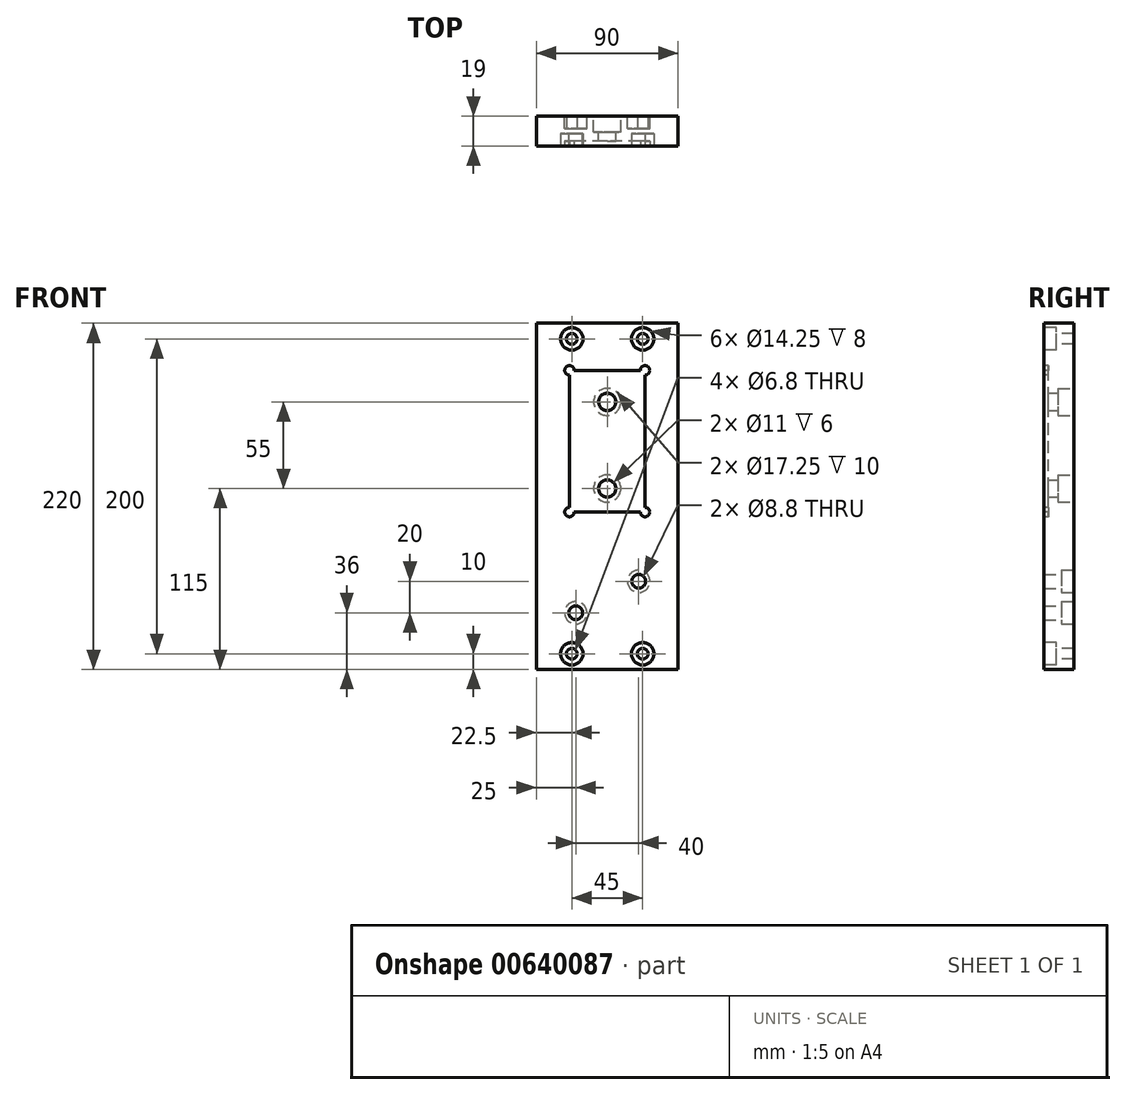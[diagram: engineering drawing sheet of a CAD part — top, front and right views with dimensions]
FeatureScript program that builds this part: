
annotation { "Feature Type Name" : "Feature", "Feature Type Description" : "" }
export const myFeature = defineFeature(function(context is Context, id is Id, definition is map)
    precondition{}
    {
        {
            var Q0;
            Q0=qCreatedBy(makeId("Front.planeOp"),FACE);
            var sketch = newSketch(context, id + "F0", { "sketchPlane" : qUnion([Q0])});
            skLineSegment(sketch, "E0.bottom", {"start": v(0, 0) * mm, "end": v(90, 0) * mm});
            skLineSegment(sketch, "E0.top", {"start": v(0, 220) * mm, "end": v(90, 220) * mm});
            skLineSegment(sketch, "E0.left", {"start": v(0, 0) * mm, "end": v(0, 220) * mm});
            skLineSegment(sketch, "E0.right", {"start": v(90, 0) * mm, "end": v(90, 220) * mm});
            skSolve(sketch);
        }
        {
            var Q0;
            Q0 = qSketchRegion(id + "F0", true);
            extrude(context, id + "F1", {"entities" : qUnion([Q0]), "depth" : 19 * mm, "offsetDistance" : 25 * mm});
        }
        {
            var Q0;
            Q0=makeQuery(id+"F1.opExtrude","CAP_FACE",FACE,{"disambiguationData":[OSD([sQuery(id+"F0.wireOp",EDGE,"E0.bottom"),sQuery(id+"F0.wireOp",EDGE,"E0.top"),sQuery(id+"F0.wireOp",EDGE,"E0.left"),sQuery(id+"F0.wireOp",EDGE,"E0.right")])],"isStart":false});
            var sketch = newSketch(context, id + "F2", { "sketchPlane" : qUnion([Q0])});
            skPoint(sketch, "E1", {"position": v(22.5, 210) * mm});
            skPoint(sketch, "E2", {"position": v(67.5, 210) * mm});
            skPoint(sketch, "E3", {"position": v(22.5, 10) * mm});
            skPoint(sketch, "E4", {"position": v(67.5, 10) * mm});
            skSolve(sketch);
        }
        {
            var Q0;
            Q0=sQuery(id+"F2.wireOp",VERTEX,"E1");
            var Q1;
            Q1=sQuery(id+"F2.wireOp",VERTEX,"E2");
            var Q2;
            Q2=sQuery(id+"F2.wireOp",VERTEX,"E3");
            var Q3;
            Q3=sQuery(id+"F2.wireOp",VERTEX,"E4");
            var Q4;
            Q4=makeQuery(id+"F1.opExtrude","SWEPT_BODY",BODY,{"disambiguationData":[OSD([sQuery(id+"F0.wireOp",EDGE,"E0.bottom"),sQuery(id+"F0.wireOp",EDGE,"E0.top"),sQuery(id+"F0.wireOp",EDGE,"E0.left"),sQuery(id+"F0.wireOp",EDGE,"E0.right")])]});
            hole(context, id + "F3", {"style" : HoleStyle.C_BORE, "endStyle" : HoleEndStyle.THROUGH, "standardTappedOrClearance" : lookupTablePath({ "standard" : "ISO", "engagement" : "75%", "pitch" : "1.25 mm", "size" : "M8", "type" : "Tapped" }), "standardBlindInLast" : lookupTablePath({ "standard" : "ISO", "engagement" : "75%", "pitch" : "1.25 mm", "size" : "M8", "type" : "Tapped" }), "holeDiameter" : 6.8 * mm, "cBoreDiameter" : 14.25 * mm, "cBoreDepth" : 8 * mm, "majorDiameter" : 8 * mm, "showTappedDepth" : true, "isTappedThrough" : true, "tappedDepth" : 14.5 * mm, "tapClearance" : 3, "startFromSketch" : true, "locations" : qUnion([Q0, Q1, Q2, Q3]), "scope" : qUnion([Q4])});
        }
        {
            var Q0;
            Q0=makeQuery(id+"F1.opExtrude","CAP_FACE",FACE,{"disambiguationData":[OSD([sQuery(id+"F0.wireOp",EDGE,"E0.bottom"),sQuery(id+"F0.wireOp",EDGE,"E0.top"),sQuery(id+"F0.wireOp",EDGE,"E0.left"),sQuery(id+"F0.wireOp",EDGE,"E0.right")])],"isStart":false});
            var sketch = newSketch(context, id + "F4", { "sketchPlane" : qUnion([Q0])});
            skPoint(sketch, "E5", {"position": v(21, 190) * mm});
            skPoint(sketch, "E6", {"position": v(69, 190) * mm});
            skPoint(sketch, "E7", {"position": v(69, 100) * mm});
            skPoint(sketch, "E8", {"position": v(21, 100) * mm});
            skLineSegment(sketch, "E9", {"start": v(21, 187) * mm, "end": v(21, 103) * mm});
            skLineSegment(sketch, "E10", {"start": v(66, 100) * mm, "end": v(24, 100) * mm});
            skLineSegment(sketch, "E11", {"start": v(69, 103) * mm, "end": v(69, 187) * mm});
            skLineSegment(sketch, "E12", {"start": v(66, 190) * mm, "end": v(24, 190) * mm});
            skArc(sketch, "E13", {"start": v(24, 190) * mm, "mid": v(18.88, 192.12) * mm, "end": v(21, 187) * mm});
            skArc(sketch, "E14", {"start": v(69, 187) * mm, "mid": v(71.12, 192.12) * mm, "end": v(66, 190) * mm});
            skArc(sketch, "E15", {"start": v(66, 100) * mm, "mid": v(71.12, 97.88) * mm, "end": v(69, 103) * mm});
            skArc(sketch, "E16", {"start": v(21, 103) * mm, "mid": v(18.88, 97.88) * mm, "end": v(24, 100) * mm});
            skSolve(sketch);
        }
        {
            var Q0;
            Q0=makeQuery(id+"F4.imprint","IMPRINT",FACE,{"disambiguationData":[TD([[makeQuery(id+"F4.imprint","IMPRINT",EDGE,{"derivedFrom":sQuery(id+"F4.wireOp",EDGE,"E9")}),1.0]])]});
            extrude(context, id + "F5", {"entities" : qUnion([Q0]), "operationType" : NewBodyOperationType.REMOVE, "oppositeDirection" : true, "depth" : 3 * mm, "offsetDistance" : 25 * mm});
        }
        {
            var Q0;
            Q0=makeQuery(id+"F1.opExtrude","CAP_FACE",FACE,{"disambiguationData":[OSD([sQuery(id+"F0.wireOp",EDGE,"E0.bottom"),sQuery(id+"F0.wireOp",EDGE,"E0.top"),sQuery(id+"F0.wireOp",EDGE,"E0.left"),sQuery(id+"F0.wireOp",EDGE,"E0.right")])],"isStart":true});
            var sketch = newSketch(context, id + "F6", { "sketchPlane" : qUnion([Q0])});
            skPoint(sketch, "E17", {"position": v(-45, 170) * mm});
            skPoint(sketch, "E17.positionSnap0", {"position": v(-45, 220) * mm});
            skPoint(sketch, "E18", {"position": v(-45, 115) * mm});
            skSolve(sketch);
        }
        {
            var Q0;
            Q0=sQuery(id+"F6.wireOp",VERTEX,"E17");
            var Q1;
            Q1=sQuery(id+"F6.wireOp",VERTEX,"E18");
            var Q2;
            Q2=makeQuery(id+"F1.opExtrude","SWEPT_BODY",BODY,{"disambiguationData":[OSD([sQuery(id+"F0.wireOp",EDGE,"E0.bottom"),sQuery(id+"F0.wireOp",EDGE,"E0.top"),sQuery(id+"F0.wireOp",EDGE,"E0.left"),sQuery(id+"F0.wireOp",EDGE,"E0.right")])]});
            hole(context, id + "F7", {"style" : HoleStyle.C_BORE, "endStyle" : HoleEndStyle.THROUGH, "standardTappedOrClearance" : lookupTablePath({ "standard" : "ISO", "fit" : "Normal", "size" : "M10", "type" : "Clearance" }), "standardBlindInLast" : lookupTablePath({ "fit" : "Standard", "standard" : "ISO", "size" : "M10", "type" : "Clearance" }), "holeDiameter" : 11 * mm, "cBoreDiameter" : 17.25 * mm, "cBoreDepth" : 10 * mm, "majorDiameter" : 10 * mm, "isTappedThrough" : true, "tappedDepth" : 14.5 * mm, "tapClearance" : 3, "startFromSketch" : true, "locations" : qUnion([Q0, Q1]), "scope" : qUnion([Q2])});
        }
        {
            var Q0;
            Q0=makeQuery(id+"F1.opExtrude","CAP_FACE",FACE,{"disambiguationData":[OSD([sQuery(id+"F0.wireOp",EDGE,"E0.bottom"),sQuery(id+"F0.wireOp",EDGE,"E0.top"),sQuery(id+"F0.wireOp",EDGE,"E0.left"),sQuery(id+"F0.wireOp",EDGE,"E0.right")])],"isStart":true});
            var sketch = newSketch(context, id + "F8", { "sketchPlane" : qUnion([Q0])});
            skPoint(sketch, "E19", {"position": v(-65, 56) * mm});
            skPoint(sketch, "E20", {"position": v(-25, 36) * mm});
            skSolve(sketch);
        }
        {
            var Q0;
            Q0=sQuery(id+"F8.wireOp",VERTEX,"E19");
            var Q1;
            Q1=sQuery(id+"F8.wireOp",VERTEX,"E20");
            var Q2;
            Q2=makeQuery(id+"F1.opExtrude","SWEPT_BODY",BODY,{"disambiguationData":[OSD([sQuery(id+"F0.wireOp",EDGE,"E0.bottom"),sQuery(id+"F0.wireOp",EDGE,"E0.top"),sQuery(id+"F0.wireOp",EDGE,"E0.left"),sQuery(id+"F0.wireOp",EDGE,"E0.right")])]});
            hole(context, id + "F9", {"style" : HoleStyle.C_BORE, "endStyle" : HoleEndStyle.THROUGH, "standardTappedOrClearance" : lookupTablePath({ "standard" : "ISO", "fit" : "Normal", "size" : "M8", "type" : "Clearance" }), "standardBlindInLast" : lookupTablePath({ "fit" : "Standard", "standard" : "ISO", "size" : "M8", "type" : "Clearance" }), "holeDiameter" : 8.8 * mm, "cBoreDiameter" : 14.25 * mm, "cBoreDepth" : 8 * mm, "majorDiameter" : 8 * mm, "isTappedThrough" : true, "tappedDepth" : 14.5 * mm, "tapClearance" : 3, "startFromSketch" : true, "locations" : qUnion([Q0, Q1]), "scope" : qUnion([Q2])});
        }
    });
